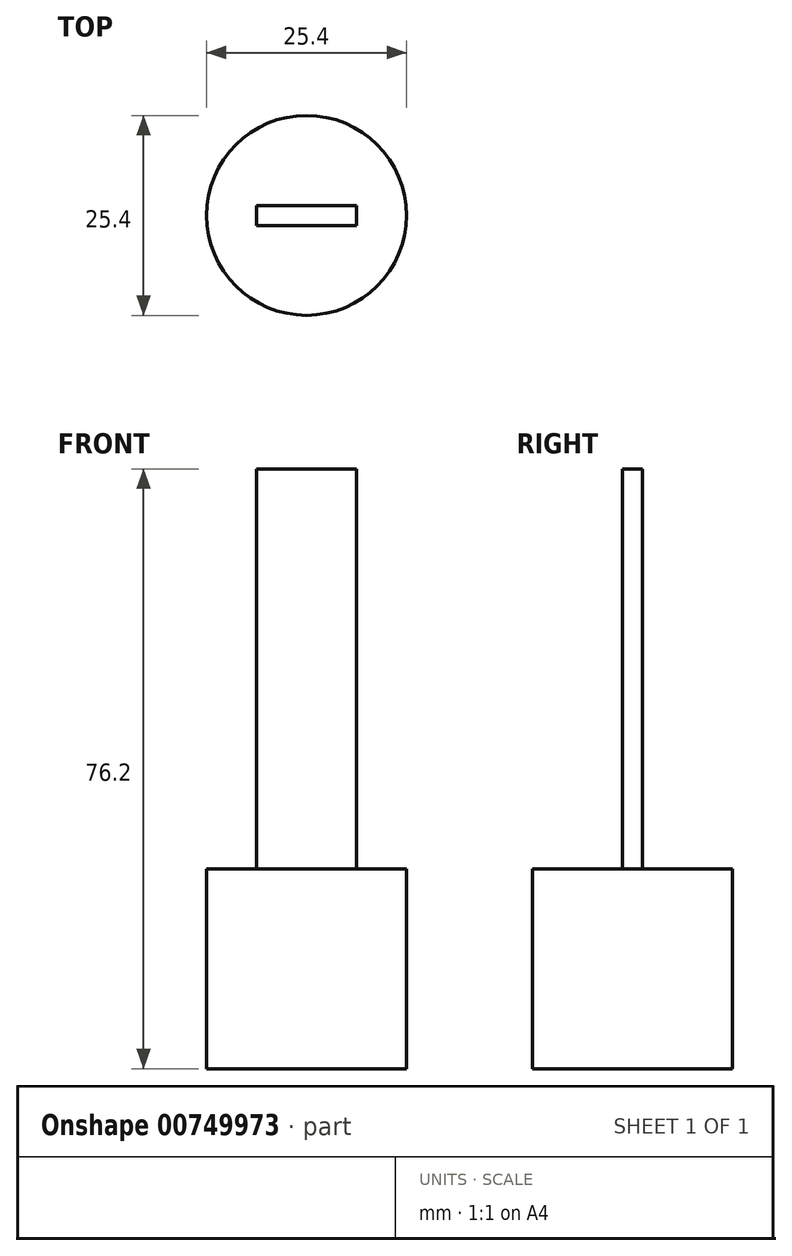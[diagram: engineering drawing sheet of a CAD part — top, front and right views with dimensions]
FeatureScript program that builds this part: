
annotation { "Feature Type Name" : "Feature", "Feature Type Description" : "" }
export const myFeature = defineFeature(function(context is Context, id is Id, definition is map)
    precondition{}
    {
        {
            var Q0;
            Q0=qCreatedBy(makeId("Top.planeOp"),FACE);
            var sketch = newSketch(context, id + "F0", { "sketchPlane" : qUnion([Q0])});
            skCircle(sketch, "E0", {"center": v(0, 0) * mm, "radius": 12.7 * mm});
            skLineSegment(sketch, "E1.bottom", {"start": v(-6.35, 1.27) * mm, "end": v(6.35, 1.27) * mm});
            skLineSegment(sketch, "E1.top", {"start": v(-6.35, -1.27) * mm, "end": v(6.35, -1.27) * mm});
            skLineSegment(sketch, "E1.left", {"start": v(-6.35, 1.27) * mm, "end": v(-6.35, -1.27) * mm});
            skLineSegment(sketch, "E1.right", {"start": v(6.35, 1.27) * mm, "end": v(6.35, -1.27) * mm});
            skSolve(sketch);
        }
        {
            var Q0;
            Q0=makeQuery(id+"F0.imprint","IMPRINT",FACE,{"disambiguationData":[TD([[makeQuery(id+"F0.imprint","IMPRINT",EDGE,{"derivedFrom":sQuery(id+"F0.wireOp",EDGE,"E0")}),1.0]])]});
            extrude(context, id + "F1", {"entities" : qUnion([Q0]), "depth" : 25.4 * mm, "offsetDistance" : 25.4 * mm});
        }
        {
            var Q0;
            Q0=makeQuery(id+"F0.imprint","IMPRINT",FACE,{"disambiguationData":[TD([[makeQuery(id+"F0.imprint","IMPRINT",EDGE,{"derivedFrom":sQuery(id+"F0.wireOp",EDGE,"E1.bottom")}),-1.0]])]});
            extrude(context, id + "F2", {"entities" : qUnion([Q0]), "operationType" : NewBodyOperationType.ADD, "depth" : 76.2 * mm, "offsetDistance" : 25.4 * mm});
        }
    });
